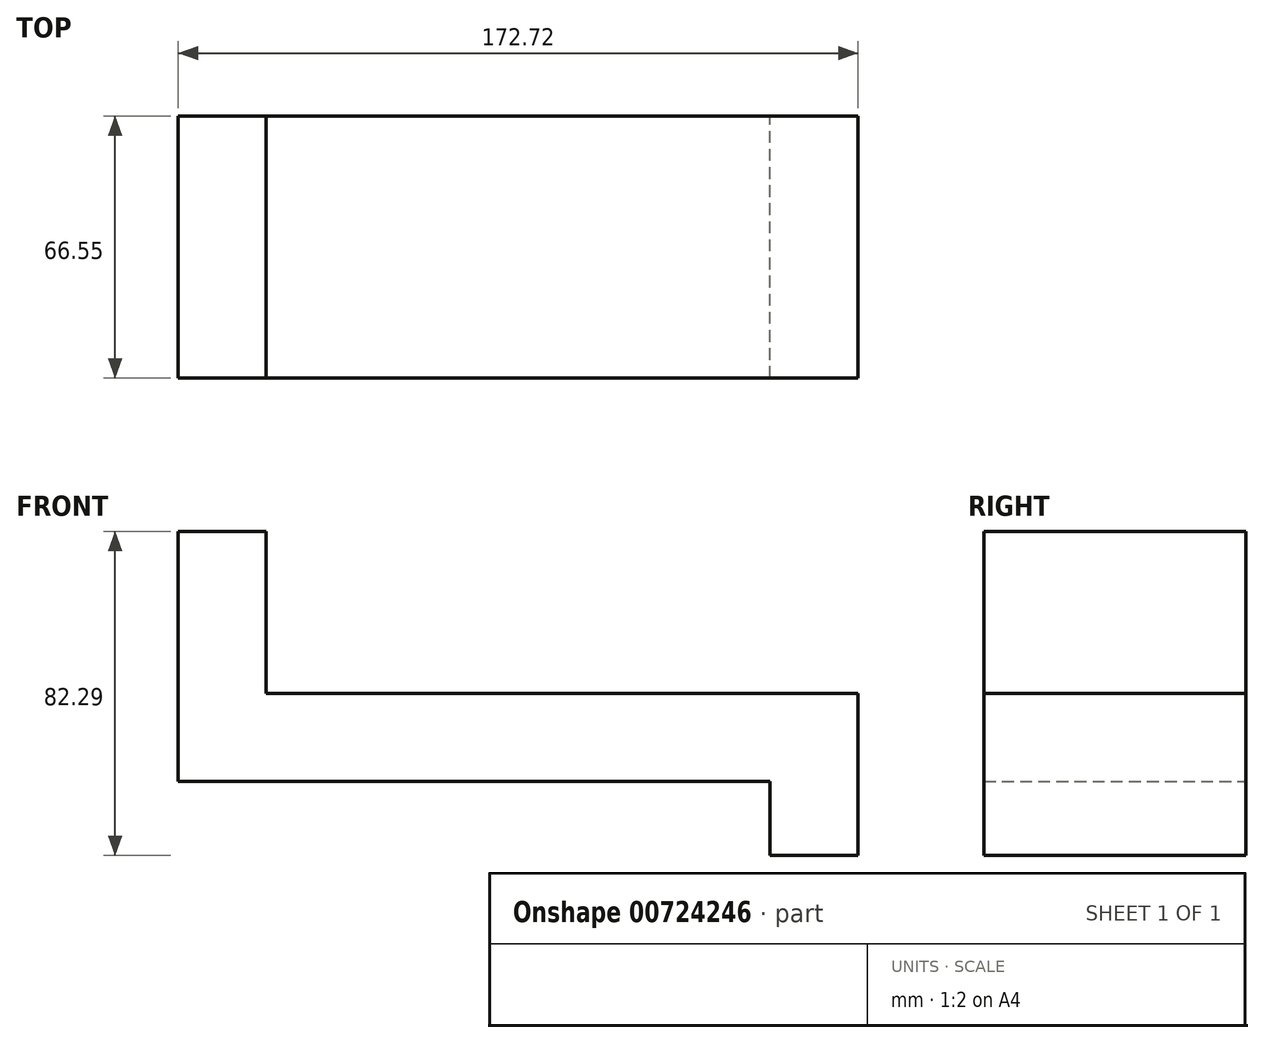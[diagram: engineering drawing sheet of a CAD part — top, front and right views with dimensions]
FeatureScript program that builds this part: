
annotation { "Feature Type Name" : "Feature", "Feature Type Description" : "" }
export const myFeature = defineFeature(function(context is Context, id is Id, definition is map)
    precondition{}
    {
        {
            var Q0;
            Q0=qCreatedBy(makeId("Front.planeOp"),FACE);
            var sketch = newSketch(context, id + "F0", { "sketchPlane" : qUnion([Q0])});
            skLineSegment(sketch, "E0", {"start": v(-59.9, 45.24) * mm, "end": v(-59.9, -18.26) * mm});
            skLineSegment(sketch, "E1", {"start": v(-59.9, -18.26) * mm, "end": v(90.48, -18.26) * mm});
            skLineSegment(sketch, "E2", {"start": v(90.48, -18.26) * mm, "end": v(90.48, -37.05) * mm});
            skLineSegment(sketch, "E3", {"start": v(90.48, -37.05) * mm, "end": v(112.83, -37.05) * mm});
            skLineSegment(sketch, "E4", {"start": v(112.83, -37.05) * mm, "end": v(112.83, 4.1) * mm});
            skLineSegment(sketch, "E5", {"start": v(112.83, 4.1) * mm, "end": v(-37.54, 4.1) * mm});
            skLineSegment(sketch, "E6", {"start": v(-37.54, 4.1) * mm, "end": v(-37.54, 45.24) * mm});
            skLineSegment(sketch, "E7", {"start": v(-37.54, 45.24) * mm, "end": v(-59.9, 45.24) * mm});
            skSolve(sketch);
        }
        {
            var Q0;
            Q0=makeQuery(id+"F0.imprint","IMPRINT",FACE,{"disambiguationData":[TD([[makeQuery(id+"F0.imprint","IMPRINT",EDGE,{"derivedFrom":sQuery(id+"F0.wireOp",EDGE,"E0")}),1.0]])]});
            extrude(context, id + "F1", {"entities" : qUnion([Q0]), "depth" : 66.55 * mm, "offsetDistance" : 25.4 * mm});
        }
    });
